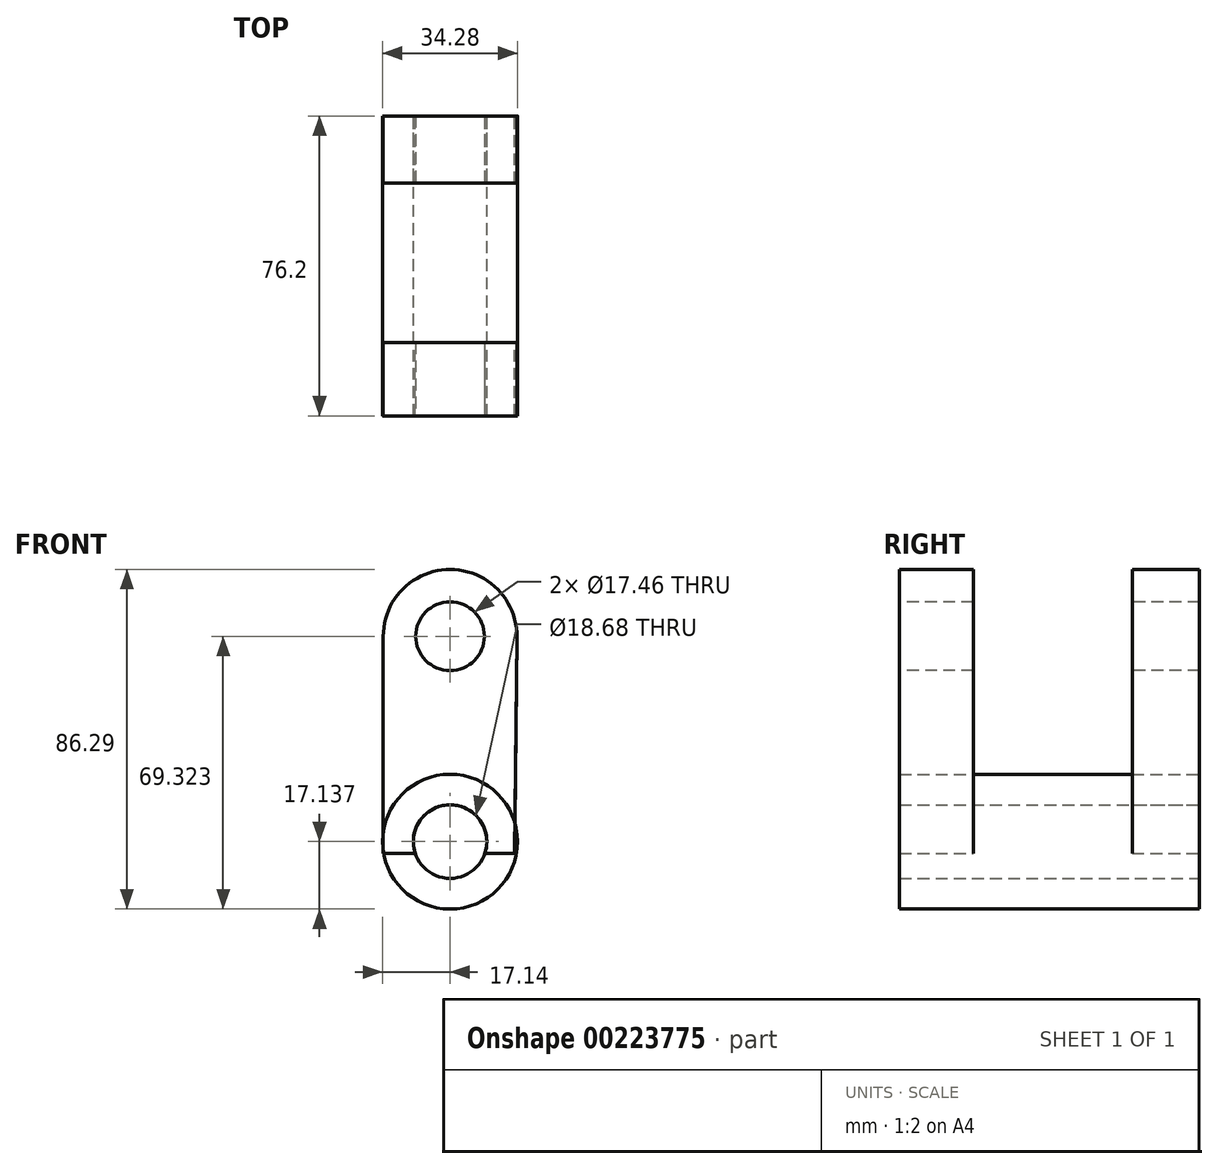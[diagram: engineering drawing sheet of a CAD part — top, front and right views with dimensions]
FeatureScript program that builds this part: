
annotation { "Feature Type Name" : "Feature", "Feature Type Description" : "" }
export const myFeature = defineFeature(function(context is Context, id is Id, definition is map)
    precondition{}
    {
        {
            var Q0;
            Q0=qCreatedBy(makeId("Front.planeOp"),FACE);
            var sketch = newSketch(context, id + "F0", { "sketchPlane" : qUnion([Q0])});
            skCircle(sketch, "E0", {"center": v(0, 37.52) * mm, "radius": 16.97 * mm});
            skLineSegment(sketch, "E1", {"start": v(-16.97, 37.52) * mm, "end": v(-16.97, -17.66) * mm});
            skLineSegment(sketch, "E2", {"start": v(-16.97, -17.66) * mm, "end": v(16.4, -17.66) * mm});
            skLineSegment(sketch, "E3", {"start": v(16.4, -17.66) * mm, "end": v(16.97, 37.52) * mm});
            skSolve(sketch);
        }
        {
            var Q0;
            Q0 = qSketchRegion(id + "F0", true);
            extrude(context, id + "F1", {"entities" : qUnion([Q0]), "depth" : 38.1 * mm, "hasSecondDirection" : true, "secondDirectionOppositeDirection" : true, "secondDirectionDepth" : 38.1 * mm});
        }
        {
            var Q0;
            Q0=qCreatedBy(makeId("Right.planeOp"),FACE);
            var sketch = newSketch(context, id + "F2", { "sketchPlane" : qUnion([Q0])});
            skLineSegment(sketch, "E4", {"start": v(-19.4, 59.7) * mm, "end": v(-19.4, -24.6) * mm});
            skLineSegment(sketch, "E5", {"start": v(-19.4, -24.6) * mm, "end": v(21.01, -24.6) * mm});
            skLineSegment(sketch, "E6", {"start": v(21.01, -24.6) * mm, "end": v(21.01, 62.7) * mm});
            skLineSegment(sketch, "E7", {"start": v(21.01, 62.7) * mm, "end": v(-19.4, 59.7) * mm});
            skSolve(sketch);
        }
        {
            var Q0;
            Q0 = qSketchRegion(id + "F2", true);
            extrude(context, id + "F3", {"entities" : qUnion([Q0]), "operationType" : NewBodyOperationType.REMOVE, "endBound" : BoundingType.THROUGH_ALL, "depth" : 25.4 * mm, "hasSecondDirection" : true, "secondDirectionBound" : SecondDirectionBoundingType.THROUGH_ALL, "secondDirectionOppositeDirection" : true, "secondDirectionDepth" : 25.4 * mm});
        }
        {
            var Q0;
            Q0=qCreatedBy(makeId("Front.planeOp"),FACE);
            var sketch = newSketch(context, id + "F4", { "sketchPlane" : qUnion([Q0])});
            skCircle(sketch, "E8", {"center": v(0, -14.66) * mm, "radius": 17.14 * mm});
            skSolve(sketch);
        }
        {
            var Q0;
            Q0 = qSketchRegion(id + "F4", true);
            extrude(context, id + "F5", {"entities" : qUnion([Q0]), "depth" : 38.1 * mm, "hasSecondDirection" : true, "secondDirectionOppositeDirection" : true, "secondDirectionDepth" : 38.1 * mm});
        }
        {
            var Q0;
            Q0=makeQuery(id+"F5.opExtrude","CAP_FACE",FACE,{"disambiguationData":[OSD([sQuery(id+"F4.wireOp",EDGE,"E8")])],"isStart":true});
            var sketch = newSketch(context, id + "F6", { "sketchPlane" : qUnion([Q0])});
            skCircle(sketch, "E9", {"center": v(0, -14.66) * mm, "radius": 9.34 * mm});
            skSolve(sketch);
        }
        {
            var Q0;
            Q0=makeQuery(id+"F6.imprint","IMPRINT",FACE,{"disambiguationData":[TD([[makeQuery(id+"F6.imprint","IMPRINT",EDGE,{"derivedFrom":sQuery(id+"F6.wireOp",EDGE,"E9")}),1.0]])]});
            extrude(context, id + "F7", {"entities" : qUnion([Q0]), "operationType" : NewBodyOperationType.REMOVE, "endBound" : BoundingType.THROUGH_ALL, "oppositeDirection" : true, "depth" : 25.4 * mm});
        }
        {
            var Q0;
            Q0=makeQuery(id+"F1.opExtrude","CAP_FACE",FACE,{"disambiguationData":[OSD([sQuery(id+"F0.wireOp",EDGE,"E0"),sQuery(id+"F0.wireOp",EDGE,"E1"),sQuery(id+"F0.wireOp",EDGE,"E2"),sQuery(id+"F0.wireOp",EDGE,"E3")])],"isStart":false});
            var sketch = newSketch(context, id + "F8", { "sketchPlane" : qUnion([Q0])});
            skCircle(sketch, "E10", {"center": v(0, 37.52) * mm, "radius": 8.73 * mm});
            skSolve(sketch);
        }
        {
            var Q0;
            Q0=makeQuery(id+"F8.imprint","IMPRINT",FACE,{"disambiguationData":[TD([[makeQuery(id+"F8.imprint","IMPRINT",EDGE,{"derivedFrom":sQuery(id+"F8.wireOp",EDGE,"E10")}),1.0]])]});
            extrude(context, id + "F9", {"entities" : qUnion([Q0]), "operationType" : NewBodyOperationType.REMOVE, "endBound" : BoundingType.THROUGH_ALL, "oppositeDirection" : true, "depth" : 25.4 * mm});
        }
    });
